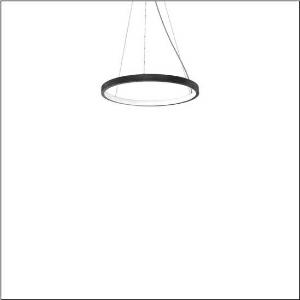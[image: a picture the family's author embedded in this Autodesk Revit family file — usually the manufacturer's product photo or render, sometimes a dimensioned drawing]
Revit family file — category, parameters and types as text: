
# Revit family: silica_r__21_ring-i_5pjbi1d3104a_e1bb
name_source: partatom
category: Lighting Fixtures
units: mm (PartAtom-declared; Revit-internal decimal feet)

## family parameters
Cut with Voids When Loaded = No
Host = Face
Light Source = No
Part Type = Normal
Room Calculation Point = No
Round Connector Dimension = Use Diameter
Shared = No

## types (1)
- Silica® 21 Ring-I (1 x LED, 3510 lm, 60 W, 4000K)
    Apparent Load = 60 VA
    CIE Flux Codes = 22 48 76 50 101
    Color Rendering = 80
    Color Temperature = 4000K
    Default Elevation = 1800 mm
    Description = Silica® 21 Ring-I, suspended luminaire, of PMMA, frosted, light emission: inner ring side luminous distribution, primary light characteristic: symmetric, installation type: suspended mounting, LED, rated luminous flux: 3.510lm, luminous efficacy: 59lm/W, light colour: 840, colour temperature: 4000K, control gear: DALI 2, with terminal, 5-pole, mains connection: 230V, AC/DC, 0/50..60Hz, rated input power: 60W, housing, of extruded aluminium section, jet black (RAL 9005), diameter: 610mm, ceiling canopy, jet black (RAL 9005), protection rating (lamp compartment): IP40, insulation class (complete): insulation class I (protective earthing), certification: CE, impact resistance: IK02, permissible operating ambient temperature: 0..+35°C, packaging unit: 1 piece
    Height = 48 mm  [stored 0.15748 ft]
    Lamp = 1 x LED
    Lamp Light Flux = 3510 lm
    Lamp Power = 60 W
    Lamp count = 1
    Length = 610 mm
    Luminous efficacy = 59 lm/W
    Manufacturer = Siteco
    ModVariant = No
    Model = 5PJBI1D3104A
    Mounting Place = Ceiling
    Mounting Type = Pendant
    Number of Poles = 1
    OnlyDefault = Yes
    Power Factor = 1
    Product Name = Silica® 21 Ring-I
    Product group = suspended luminaire
    ProductGroupID = 904
    Protection Class = Protection class I
    Protection Degree = IP 40
    RLX_Detail_Level = 1
    RLX_Emergency_Light_Flux = 0 lm
    RLX_Emergency_Type = 0
    RLX_Emergency_Type_DB = No
    RlxData = <blob elided: 12369 chars, md5=abf20c1a>
    Socket = socket
    Standby Power = 0 W
    System Light Flux = 3510 lm
    System Power = 60 W
    Type Comments = Product without accessories
    Type Image = l_1258361.jpg
    URL = http://relux.com
    VarID = ---
    Voltage = 0 V
    Weight = 0.00 kg
    Width = 0 mm  [stored 0 ft]

note: [stored X ft] marks values corroborated as IEEE doubles in the binary element streams (Revit-internal decimal feet)

## geometry (parser evidence)
native form markers: Sweep x12
no freeform markers — native parametric forms only
